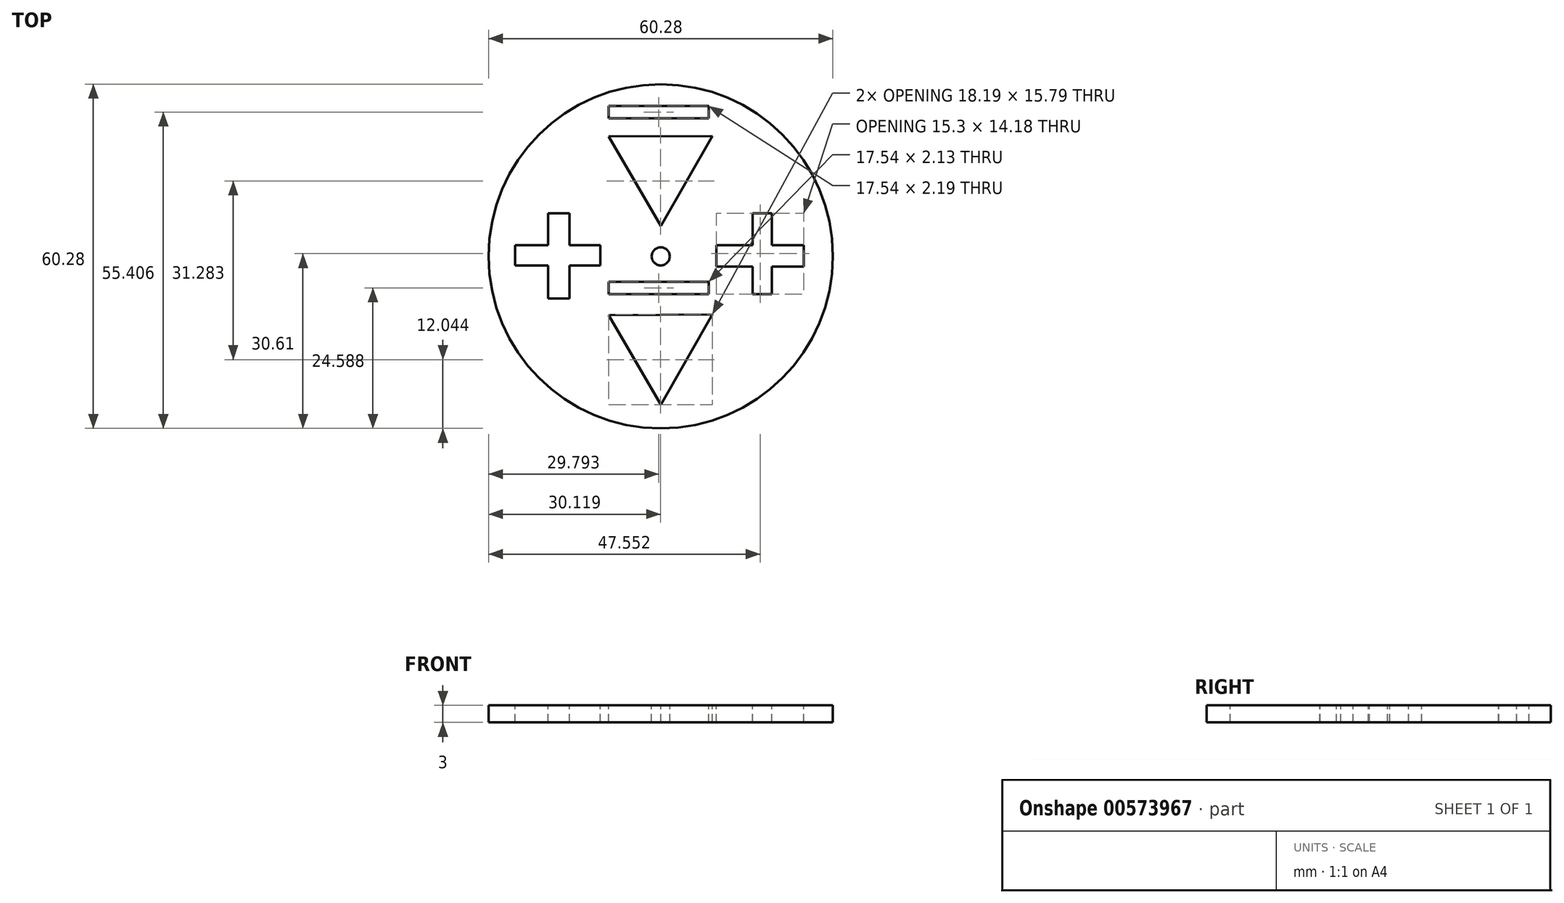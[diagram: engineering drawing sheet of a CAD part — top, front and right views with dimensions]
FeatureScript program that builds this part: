
annotation { "Feature Type Name" : "Feature", "Feature Type Description" : "" }
export const myFeature = defineFeature(function(context is Context, id is Id, definition is map)
    precondition{}
    {
        {
            var Q0;
            Q0=qCreatedBy(makeId("Top.planeOp"),FACE);
            var sketch = newSketch(context, id + "F0", { "sketchPlane" : qUnion([Q0])});
            skCircle(sketch, "E0", {"center": v(0, 0) * mm, "radius": 30.14 * mm});
            skSolve(sketch);
        }
        {
            var Q0;
            Q0 = qSketchRegion(id + "F0", true);
            extrude(context, id + "F1", {"entities" : qUnion([Q0]), "depth" : 3 * mm, "offsetDistance" : 25 * mm});
        }
        {
            var Q0;
            Q0=makeQuery(id+"F1.opExtrude","CAP_FACE",FACE,{"disambiguationData":[OSD([sQuery(id+"F0.wireOp",EDGE,"E0")])],"isStart":false});
            var sketch = newSketch(context, id + "F2", { "sketchPlane" : qUnion([Q0])});
            skCircle(sketch, "E1", {"center": v(0, 0) * mm, "radius": 1.6 * mm});
            skSolve(sketch);
        }
        {
            var Q0;
            Q0 = qSketchRegion(id + "F2", true);
            extrude(context, id + "F3", {"entities" : qUnion([Q0]), "operationType" : NewBodyOperationType.REMOVE, "oppositeDirection" : true, "depth" : 25 * mm, "offsetDistance" : 25 * mm});
        }
        {
            var Q0;
            Q0=makeQuery(id+"F1.opExtrude","CAP_FACE",FACE,{"disambiguationData":[OSD([sQuery(id+"F0.wireOp",EDGE,"E0")])],"isStart":false});
            var sketch = newSketch(context, id + "F4", { "sketchPlane" : qUnion([Q0])});
            skCircle(sketch, "E2.cCircle", {"center": v(0, 15.8) * mm, "radius": 5.25 * mm, "construction": true});
            skLineSegment(sketch, "E2.0", {"start": v(9.07, 21.08) * mm, "end": v(0.04, 5.3) * mm});
            skLineSegment(sketch, "E2.1", {"start": v(0.04, 5.3) * mm, "end": v(-9.12, 21) * mm});
            skLineSegment(sketch, "E2.2", {"start": v(-9.12, 21) * mm, "end": v(9.07, 21.08) * mm});
            skPoint(sketch, "E2.0.midPoint", {"position": v(4.56, 13.19) * mm});
            skCircle(sketch, "E3.cCircle", {"center": v(0, -15.49) * mm, "radius": 5.25 * mm, "construction": true});
            skLineSegment(sketch, "E3.0", {"start": v(9.07, -10.2) * mm, "end": v(0.04, -26) * mm});
            skLineSegment(sketch, "E3.1", {"start": v(0.04, -26) * mm, "end": v(-9.12, -10.27) * mm});
            skLineSegment(sketch, "E3.2", {"start": v(-9.12, -10.27) * mm, "end": v(9.07, -10.2) * mm});
            skPoint(sketch, "E3.0.midPoint", {"position": v(4.56, -18.1) * mm});
            skSolve(sketch);
        }
        {
            var Q0;
            Q0 = qSketchRegion(id + "F4", true);
            extrude(context, id + "F5", {"entities" : qUnion([Q0]), "operationType" : NewBodyOperationType.REMOVE, "oppositeDirection" : true, "depth" : 25 * mm, "offsetDistance" : 25 * mm});
        }
        {
            var Q0;
            Q0=makeQuery(id+"F1.opExtrude","CAP_FACE",FACE,{"disambiguationData":[OSD([sQuery(id+"F0.wireOp",EDGE,"E0")])],"isStart":false});
            var sketch = newSketch(context, id + "F6", { "sketchPlane" : qUnion([Q0])});
            skLineSegment(sketch, "E4.bottom", {"start": v(-19.7, 7.56) * mm, "end": v(-15.98, 7.56) * mm});
            skLineSegment(sketch, "E4.top", {"start": v(-19.7, -7.36) * mm, "end": v(-15.98, -7.36) * mm});
            skLineSegment(sketch, "E4.left", {"start": v(-19.7, 7.56) * mm, "end": v(-19.7, -7.36) * mm});
            skLineSegment(sketch, "E4.right", {"start": v(-15.98, 7.56) * mm, "end": v(-15.98, -7.36) * mm});
            skSolve(sketch);
        }
        {
            var Q0;
            Q0 = qSketchRegion(id + "F6", true);
            extrude(context, id + "F7", {"entities" : qUnion([Q0]), "operationType" : NewBodyOperationType.REMOVE, "oppositeDirection" : true, "depth" : 25 * mm, "offsetDistance" : 25 * mm});
        }
        {
            var Q0;
            Q0=makeQuery(id+"F1.opExtrude","CAP_FACE",FACE,{"disambiguationData":[OSD([sQuery(id+"F0.wireOp",EDGE,"E0")])],"isStart":false});
            var sketch = newSketch(context, id + "F8", { "sketchPlane" : qUnion([Q0])});
            skLineSegment(sketch, "E5.bottom", {"start": v(-25.5, 1.96) * mm, "end": v(-10.57, 1.96) * mm});
            skLineSegment(sketch, "E5.top", {"start": v(-25.5, -1.58) * mm, "end": v(-10.57, -1.58) * mm});
            skLineSegment(sketch, "E5.left", {"start": v(-25.5, 1.96) * mm, "end": v(-25.5, -1.58) * mm});
            skLineSegment(sketch, "E5.right", {"start": v(-10.57, 1.96) * mm, "end": v(-10.57, -1.58) * mm});
            skSolve(sketch);
        }
        {
            var Q0;
            Q0 = qSketchRegion(id + "F8", true);
            extrude(context, id + "F9", {"entities" : qUnion([Q0]), "operationType" : NewBodyOperationType.REMOVE, "oppositeDirection" : true, "depth" : 25 * mm, "offsetDistance" : 25 * mm});
        }
        {
            var Q0;
            Q0=makeQuery(id+"F1.opExtrude","CAP_FACE",FACE,{"disambiguationData":[OSD([sQuery(id+"F0.wireOp",EDGE,"E0")])],"isStart":false});
            var sketch = newSketch(context, id + "F10", { "sketchPlane" : qUnion([Q0])});
            skPoint(sketch, "E6.firstSnap0", {"position": v(-17.84, 7.56) * mm});
            skLineSegment(sketch, "E6.bottom", {"start": v(16.1, 7.56) * mm, "end": v(19.46, 7.56) * mm});
            skLineSegment(sketch, "E6.top", {"start": v(16.1, -6.62) * mm, "end": v(19.46, -6.62) * mm});
            skLineSegment(sketch, "E6.left", {"start": v(16.1, 7.56) * mm, "end": v(16.1, -6.62) * mm});
            skLineSegment(sketch, "E6.right", {"start": v(19.46, 7.56) * mm, "end": v(19.46, -6.62) * mm});
            skSolve(sketch);
        }
        {
            var Q0;
            Q0 = qSketchRegion(id + "F10", true);
            extrude(context, id + "F11", {"entities" : qUnion([Q0]), "operationType" : NewBodyOperationType.REMOVE, "oppositeDirection" : true, "depth" : 25 * mm, "offsetDistance" : 25 * mm});
        }
        {
            var Q0;
            Q0=makeQuery(id+"F1.opExtrude","CAP_FACE",FACE,{"disambiguationData":[OSD([sQuery(id+"F0.wireOp",EDGE,"E0")])],"isStart":false});
            var sketch = newSketch(context, id + "F12", { "sketchPlane" : qUnion([Q0])});
            skLineSegment(sketch, "E7.bottom", {"start": v(9.76, 1.96) * mm, "end": v(25.06, 1.96) * mm});
            skLineSegment(sketch, "E7.top", {"start": v(9.76, -1.77) * mm, "end": v(25.06, -1.77) * mm});
            skLineSegment(sketch, "E7.left", {"start": v(9.76, 1.96) * mm, "end": v(9.76, -1.77) * mm});
            skLineSegment(sketch, "E7.right", {"start": v(25.06, 1.96) * mm, "end": v(25.06, -1.77) * mm});
            skSolve(sketch);
        }
        {
            var Q0;
            Q0 = qSketchRegion(id + "F12", true);
            extrude(context, id + "F13", {"entities" : qUnion([Q0]), "operationType" : NewBodyOperationType.REMOVE, "oppositeDirection" : true, "depth" : 25 * mm, "offsetDistance" : 25 * mm});
        }
        {
            var Q0;
            Q0=makeQuery(id+"F1.opExtrude","CAP_FACE",FACE,{"disambiguationData":[OSD([sQuery(id+"F0.wireOp",EDGE,"E0")])],"isStart":false});
            var sketch = newSketch(context, id + "F14", { "sketchPlane" : qUnion([Q0])});
            skLineSegment(sketch, "E8.bottom", {"start": v(-9.12, 24.17) * mm, "end": v(8.42, 24.17) * mm});
            skLineSegment(sketch, "E8.top", {"start": v(-9.12, 26.36) * mm, "end": v(8.42, 26.36) * mm});
            skLineSegment(sketch, "E8.left", {"start": v(-9.12, 24.17) * mm, "end": v(-9.12, 26.36) * mm});
            skLineSegment(sketch, "E8.right", {"start": v(8.42, 24.17) * mm, "end": v(8.42, 26.36) * mm});
            skLineSegment(sketch, "E9.bottom", {"start": v(-9.12, -6.62) * mm, "end": v(8.42, -6.62) * mm});
            skLineSegment(sketch, "E9.top", {"start": v(-9.12, -4.48) * mm, "end": v(8.42, -4.48) * mm});
            skLineSegment(sketch, "E9.left", {"start": v(-9.12, -6.62) * mm, "end": v(-9.12, -4.48) * mm});
            skLineSegment(sketch, "E9.right", {"start": v(8.42, -6.62) * mm, "end": v(8.42, -4.48) * mm});
            skSolve(sketch);
        }
        {
            var Q0;
            Q0 = qSketchRegion(id + "F14", true);
            extrude(context, id + "F15", {"entities" : qUnion([Q0]), "operationType" : NewBodyOperationType.REMOVE, "oppositeDirection" : true, "depth" : 25 * mm, "offsetDistance" : 25 * mm});
        }
    });
